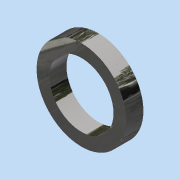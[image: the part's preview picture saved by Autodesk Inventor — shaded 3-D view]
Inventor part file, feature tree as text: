
AUTODESK INVENTOR PART (.ipt)
format: ipt  version: 2015 (Build 190159000, 159)  size: 121,344 bytes
history: native  units: in
note: dims shown in document units (in); Inventor stores cm internally (conversion verified against a paired STEP export)
features: extrude x1, sketch x1
ambient origin geometry x8: Origin, YZ Plane, XZ Plane, XY Plane, X Axis, Y Axis, Z Axis, Center Point
bodies: Body1 (feature_tree)
feature tree (2):
  extrude  "Extrusion1"  Depth=0.1575in
  sketch  "Sketch1"  dims[d0=0.5906in d1=0.8268in d2=0.1575in d3=0.0in]
